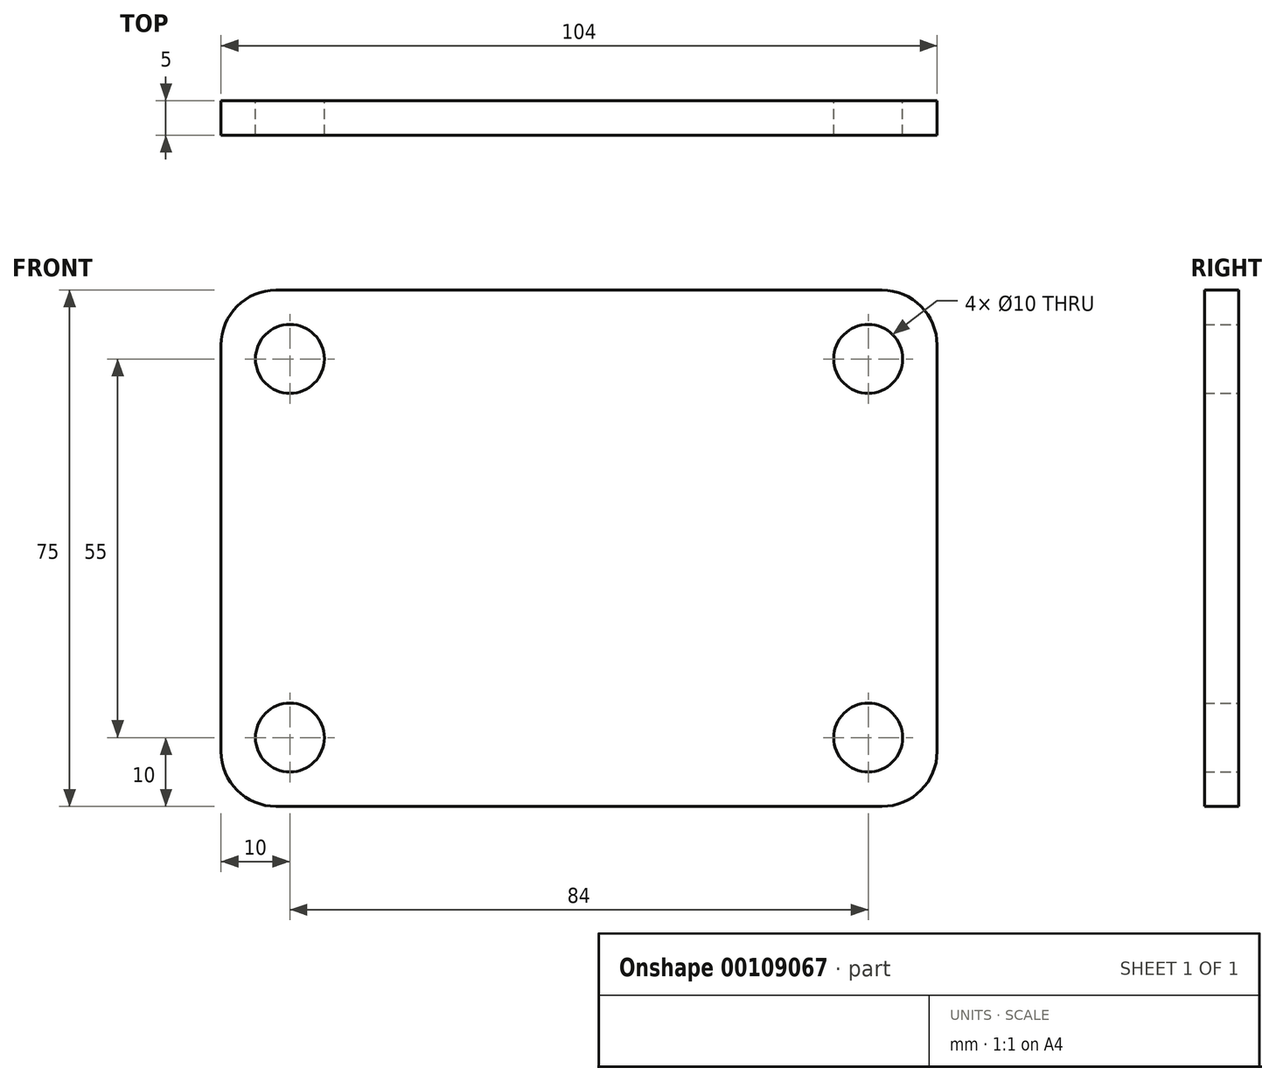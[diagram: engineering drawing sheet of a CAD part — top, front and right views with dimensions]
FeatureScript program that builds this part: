
annotation { "Feature Type Name" : "Feature", "Feature Type Description" : "" }
export const myFeature = defineFeature(function(context is Context, id is Id, definition is map)
    precondition{}
    {
        {
            var Q0;
            Q0=qCreatedBy(makeId("Front.planeOp"),FACE);
            var sketch = newSketch(context, id + "F0", { "sketchPlane" : qUnion([Q0])});
            skLineSegment(sketch, "E0.bottom", {"start": v(42, 27.5) * mm, "end": v(-42, 27.5) * mm, "construction": true});
            skLineSegment(sketch, "E0.top", {"start": v(42, -27.5) * mm, "end": v(-42, -27.5) * mm, "construction": true});
            skLineSegment(sketch, "E0.left", {"start": v(42, 27.5) * mm, "end": v(42, -27.5) * mm, "construction": true});
            skLineSegment(sketch, "E0.right", {"start": v(-42, 27.5) * mm, "end": v(-42, -27.5) * mm, "construction": true});
            skPoint(sketch, "E0.middle", {"position": v(0, 0) * mm});
            skLineSegment(sketch, "E1.bottom", {"start": v(44, -37.5) * mm, "end": v(-44, -37.5) * mm});
            skLineSegment(sketch, "E1.top", {"start": v(44, 37.5) * mm, "end": v(-44, 37.5) * mm});
            skLineSegment(sketch, "E1.left", {"start": v(52, -29.5) * mm, "end": v(52, 29.5) * mm});
            skLineSegment(sketch, "E1.right", {"start": v(-52, -29.5) * mm, "end": v(-52, 29.5) * mm});
            skPoint(sketch, "E2.visualSharp", {"position": v(-52, 37.5) * mm});
            skArc(sketch, "E2.filletArc", {"start": v(-44, 37.5) * mm, "mid": v(-49.66, 35.16) * mm, "end": v(-52, 29.5) * mm});
            skPoint(sketch, "E3.visualSharp", {"position": v(52, -37.5) * mm});
            skArc(sketch, "E3.filletArc", {"start": v(44, -37.5) * mm, "mid": v(49.66, -35.16) * mm, "end": v(52, -29.5) * mm});
            skPoint(sketch, "E4.visualSharp", {"position": v(-52, -37.5) * mm});
            skArc(sketch, "E4.filletArc", {"start": v(-52, -29.5) * mm, "mid": v(-49.66, -35.16) * mm, "end": v(-44, -37.5) * mm});
            skPoint(sketch, "E5.visualSharp", {"position": v(52, 37.5) * mm});
            skArc(sketch, "E5.filletArc", {"start": v(52, 29.5) * mm, "mid": v(49.66, 35.16) * mm, "end": v(44, 37.5) * mm});
            skCircle(sketch, "E6", {"center": v(-42, 27.5) * mm, "radius": 5 * mm});
            skCircle(sketch, "E7", {"center": v(42, 27.5) * mm, "radius": 5 * mm});
            skCircle(sketch, "E8", {"center": v(42, -27.5) * mm, "radius": 5 * mm});
            skCircle(sketch, "E9", {"center": v(-42, -27.5) * mm, "radius": 5 * mm});
            skSolve(sketch);
        }
        {
            var Q0;
            Q0=makeQuery(id+"F0.imprint","IMPRINT",FACE,{"disambiguationData":[TD([[makeQuery(id+"F0.imprint","IMPRINT",EDGE,{"derivedFrom":sQuery(id+"F0.wireOp",EDGE,"E1.bottom")}),-1.0]])]});
            extrude(context, id + "F1", {"entities" : qUnion([Q0]), "depth" : 5 * mm});
        }
    });
